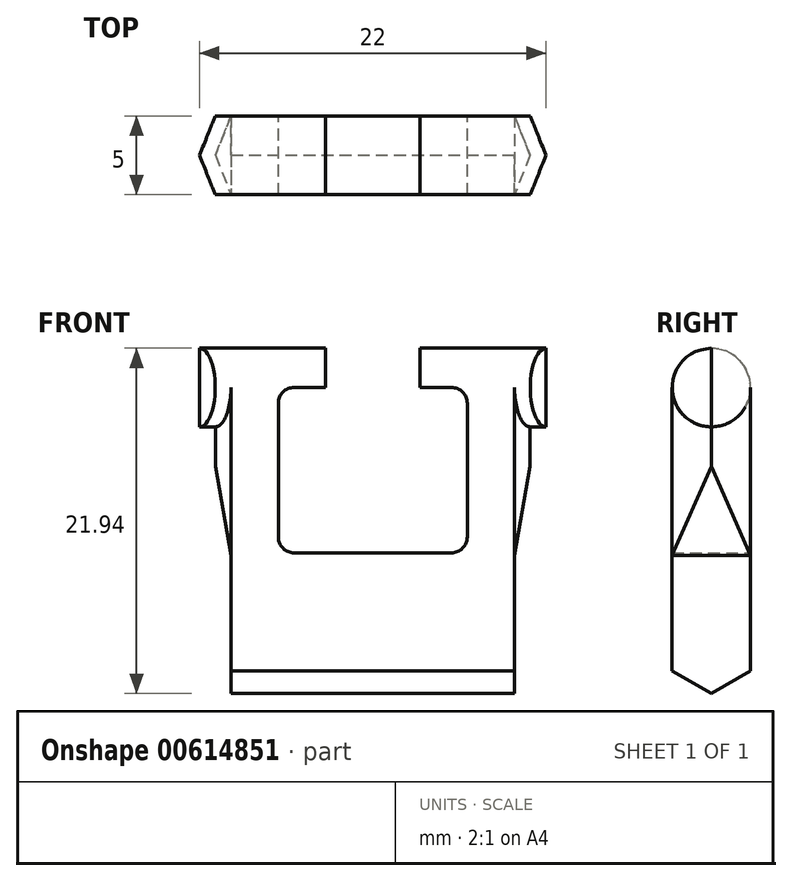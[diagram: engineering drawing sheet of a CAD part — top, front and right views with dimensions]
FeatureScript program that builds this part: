
annotation { "Feature Type Name" : "Feature", "Feature Type Description" : "" }
export const myFeature = defineFeature(function(context is Context, id is Id, definition is map)
    precondition{}
    {
        {
            var Q0;
            Q0=qCreatedBy(makeId("Front.planeOp"),FACE);
            var sketch = newSketch(context, id + "F0", { "sketchPlane" : qUnion([Q0])});
            skLineSegment(sketch, "E0", {"start": v(0, 0) * mm, "end": v(9, 0) * mm});
            skLineSegment(sketch, "E1", {"start": v(9, 0) * mm, "end": v(9, 14) * mm});
            skLineSegment(sketch, "E2", {"start": v(9, 14) * mm, "end": v(6, 14) * mm});
            skLineSegment(sketch, "E3", {"start": v(6, 14) * mm, "end": v(6, 3.5) * mm});
            skLineSegment(sketch, "E4", {"start": v(6, 3.5) * mm, "end": v(0, 3.5) * mm});
            skLineSegment(sketch, "E5", {"start": v(0, 3.5) * mm, "end": v(0, 0) * mm});
            skSolve(sketch);
        }
        {
            var Q0;
            Q0=qCreatedBy(makeId("Right.planeOp"),FACE);
            var sketch = newSketch(context, id + "F1", { "sketchPlane" : qUnion([Q0])});
            skCircle(sketch, "E6", {"center": v(0, 14) * mm, "radius": 2.5 * mm});
            skLineSegment(sketch, "E7", {"start": v(-2.5, 14) * mm, "end": v(2.5, 14) * mm});
            skSolve(sketch);
        }
        {
            var Q0;
            Q0=qSketchRegion(id+"F0",true);
            extrude(context, id + "F2", {"entities" : qUnion([Q0]), "endBound" : BoundingType.SYMMETRIC, "depth" : 5 * mm, "offsetDistance" : 25 * mm});
        }
        {
            var Q0;
            Q0=qSketchRegion(id+"F1",true);
            extrude(context, id + "F3", {"entities" : qUnion([Q0]), "operationType" : NewBodyOperationType.ADD, "depth" : 10 * mm, "offsetDistance" : 25 * mm});
        }
        {
            var Q0;
            Q0=qSketchRegion(id+"F1",true);
            extrude(context, id + "F4", {"entities" : qUnion([Q0]), "operationType" : NewBodyOperationType.REMOVE, "depth" : 3 * mm, "offsetDistance" : 25 * mm});
        }
        {
            var Q0;
            {var subQ0=sQuery(id+"F1.wireOp",EDGE,"E7");Q0=makeQuery(id+"F1.imprint","IMPRINT",FACE,{"disambiguationData":[TD([[makeQuery(id+"F1.imprint","IMPRINT",EDGE,{"derivedFrom":subQ0}),-1.0]])]});}
            extrude(context, id + "F5", {"entities" : qUnion([Q0]), "operationType" : NewBodyOperationType.REMOVE, "depth" : 6 * mm, "offsetDistance" : 25 * mm});
        }
        {
            var Q0;
            Q0=makeQuery(id+"F5.boolean.opBoolean","COPY",EDGE,{"derivedFrom":makeQuery(id+"F5.opExtrude","CAP_EDGE",EDGE,{"disambiguationData":[OSD([sQuery(id+"F1.wireOp",EDGE,"E7")])],"isStart":false})});
            var Q1;
            Q1=makeQuery(id+"F2.opExtrude","SWEPT_EDGE",EDGE,{"disambiguationData":[OSD([sQuery(id+"F0.wireOp",EDGE,"E3"),sQuery(id+"F0.wireOp",EDGE,"E4")])]});
            fillet(context, id + "F6", {"entities" : qUnion([Q0, Q1]), "radius" : 1 * mm, "tangentPropagation" : true, "allowEdgeOverflow" : false});
        }
        {
            var Q0;
            Q0=qCreatedBy(makeId("Top.planeOp"),FACE);
            var sketch = newSketch(context, id + "F7", { "sketchPlane" : qUnion([Q0])});
            skLineSegment(sketch, "E8", {"start": v(9, -2.5) * mm, "end": v(10, 0) * mm});
            skLineSegment(sketch, "E9", {"start": v(9, 2.5) * mm, "end": v(10, 0) * mm});
            skLineSegment(sketch, "E10", {"start": v(9, -2.5) * mm, "end": v(9, 2.5) * mm});
            skLineSegment(sketch, "E11", {"start": v(10, -2.5) * mm, "end": v(11, 0) * mm});
            skLineSegment(sketch, "E12", {"start": v(10, 2.5) * mm, "end": v(11, 0) * mm});
            skLineSegment(sketch, "E13", {"start": v(10, -2.5) * mm, "end": v(11.5, -2.5) * mm});
            skLineSegment(sketch, "E14", {"start": v(11.5, -2.5) * mm, "end": v(11.5, 2.5) * mm});
            skLineSegment(sketch, "E15", {"start": v(11.5, 2.5) * mm, "end": v(10, 2.5) * mm});
            skSolve(sketch);
        }
        {
            var Q0;
            Q0=makeQuery(id+"F7.imprint","IMPRINT",FACE,{"disambiguationData":[TD([[makeQuery(id+"F7.imprint","IMPRINT",EDGE,{"derivedFrom":sQuery(id+"F7.wireOp",EDGE,"E8")}),1.0]])]});
            extrude(context, id + "F8", {"entities" : qUnion([Q0]), "operationType" : NewBodyOperationType.ADD, "depth" : 14 * mm, "offsetDistance" : 25 * mm});
        }
        {
            var Q0;
            Q0=makeQuery(id+"F7.imprint","IMPRINT",FACE,{"disambiguationData":[TD([[makeQuery(id+"F7.imprint","IMPRINT",EDGE,{"derivedFrom":sQuery(id+"F7.wireOp",EDGE,"E8")}),1.0]])]});
            extrude(context, id + "F9", {"entities" : qUnion([Q0]), "operationType" : NewBodyOperationType.REMOVE, "depth" : 9 * mm, "offsetDistance" : 25 * mm});
        }
        {
            var Q0;
            Q0=makeQuery(id+"F3.opExtrude","CAP_FACE",FACE,{"disambiguationData":[OSD([sQuery(id+"F1.wireOp",EDGE,"E6")])],"isStart":false});
            extrude(context, id + "F10", {"entities" : qUnion([Q0]), "operationType" : NewBodyOperationType.ADD, "depth" : 1 * mm, "offsetDistance" : 25 * mm});
        }
        {
            var Q0;
            Q0=makeQuery(id+"F7.imprint","IMPRINT",FACE,{"disambiguationData":[TD([[makeQuery(id+"F7.imprint","IMPRINT",EDGE,{"derivedFrom":sQuery(id+"F7.wireOp",EDGE,"E11")}),-1.0]])]});
            extrude(context, id + "F11", {"entities" : qUnion([Q0]), "operationType" : NewBodyOperationType.REMOVE, "depth" : 16.5 * mm, "offsetDistance" : 25 * mm});
        }
        {
            var Q0;
            Q0=makeQuery(id+"F9.boolean.opBoolean","COPY",EDGE,{"derivedFrom":makeQuery(id+"F9.opExtrude","CAP_EDGE",EDGE,{"disambiguationData":[OSD([sQuery(id+"F7.wireOp",EDGE,"E10")])],"isStart":false})});
            chamfer(context, id + "F12", {"entities" : qUnion([Q0]), "chamferType" : ChamferType.OFFSET_ANGLE, "width" : 1 * mm, "oppositeDirection" : false, "angle" : 80 * degree, "tangentPropagation" : true});
        }
        {
            var Q0;
            Q0=makeQuery(id+"F2.opExtrude","SWEPT_BODY",BODY,{"disambiguationData":[OSD([sQuery(id+"F0.wireOp",EDGE,"E0"),sQuery(id+"F0.wireOp",EDGE,"E1"),sQuery(id+"F0.wireOp",EDGE,"E2"),sQuery(id+"F0.wireOp",EDGE,"E3"),sQuery(id+"F0.wireOp",EDGE,"E4"),sQuery(id+"F0.wireOp",EDGE,"E5")])]});
            var Q1;
            Q1=makeQuery(id+"F2.opExtrude","SWEPT_FACE",FACE,{"disambiguationData":[OSD([sQuery(id+"F0.wireOp",EDGE,"E5")])]});
            mirror(context, id + "F13", {"operationType" : NewBodyOperationType.ADD, "entities" : qUnion([Q0]), "mirrorPlane" : qUnion([Q1])});
        }
        {
            var Q0;
            {var subQ0=makeQuery(id+"F8.boolean.opBoolean","MERGE",FACE,{"derivedFrom":[makeQuery(id+"F2.opExtrude","SWEPT_FACE",FACE,{"disambiguationData":[OSD([sQuery(id+"F0.wireOp",EDGE,"E0")])]}),makeQuery(id+"F8.opExtrude","CAP_FACE",FACE,{"disambiguationData":[OSD([sQuery(id+"F7.wireOp",EDGE,"E8"),sQuery(id+"F7.wireOp",EDGE,"E9"),sQuery(id+"F7.wireOp",EDGE,"E10")])],"isStart":true})]});Q0=makeQuery(id+"F13.boolean.opBoolean","MERGE",FACE,{"derivedFrom":[subQ0,makeQuery(id+"F13.opPattern","COPY",FACE,{"derivedFrom":subQ0,"instanceName":"1"})]});}
            extrude(context, id + "F14", {"entities" : qUnion([Q0]), "operationType" : NewBodyOperationType.ADD, "depth" : 6 * mm, "offsetDistance" : 25 * mm});
        }
        {
            var Q0;
            {var subQ0=sQuery(id+"F0.wireOp",EDGE,"E0");var subQ1=makeQuery(id+"F2.opExtrude","CAP_EDGE",EDGE,{"disambiguationData":[OSD([subQ0])],"isStart":false});Q0=makeQuery(id+"F14.opExtrude","CAP_EDGE",EDGE,{"disambiguationData":[OSD([subQ0]),TDD([makeQuery(id+"F13.boolean.opBoolean","MERGE",EDGE,{"derivedFrom":[subQ1,makeQuery(id+"F13.opPattern","COPY",EDGE,{"derivedFrom":subQ1,"instanceName":"1"})]})])],"isStart":false});}
            var Q1;
            {var subQ0=sQuery(id+"F0.wireOp",EDGE,"E0");var subQ1=makeQuery(id+"F2.opExtrude","CAP_EDGE",EDGE,{"disambiguationData":[OSD([subQ0])],"isStart":true});Q1=makeQuery(id+"F14.opExtrude","CAP_EDGE",EDGE,{"disambiguationData":[OSD([subQ0]),TDD([makeQuery(id+"F13.boolean.opBoolean","MERGE",EDGE,{"derivedFrom":[subQ1,makeQuery(id+"F13.opPattern","COPY",EDGE,{"derivedFrom":subQ1,"instanceName":"1"})]})])],"isStart":false});}
            chamfer(context, id + "F15", {"entities" : qUnion([Q0, Q1]), "chamferType" : ChamferType.OFFSET_ANGLE, "width" : 2 * mm, "oppositeDirection" : false, "angle" : 60 * degree, "tangentPropagation" : true});
        }
    });
